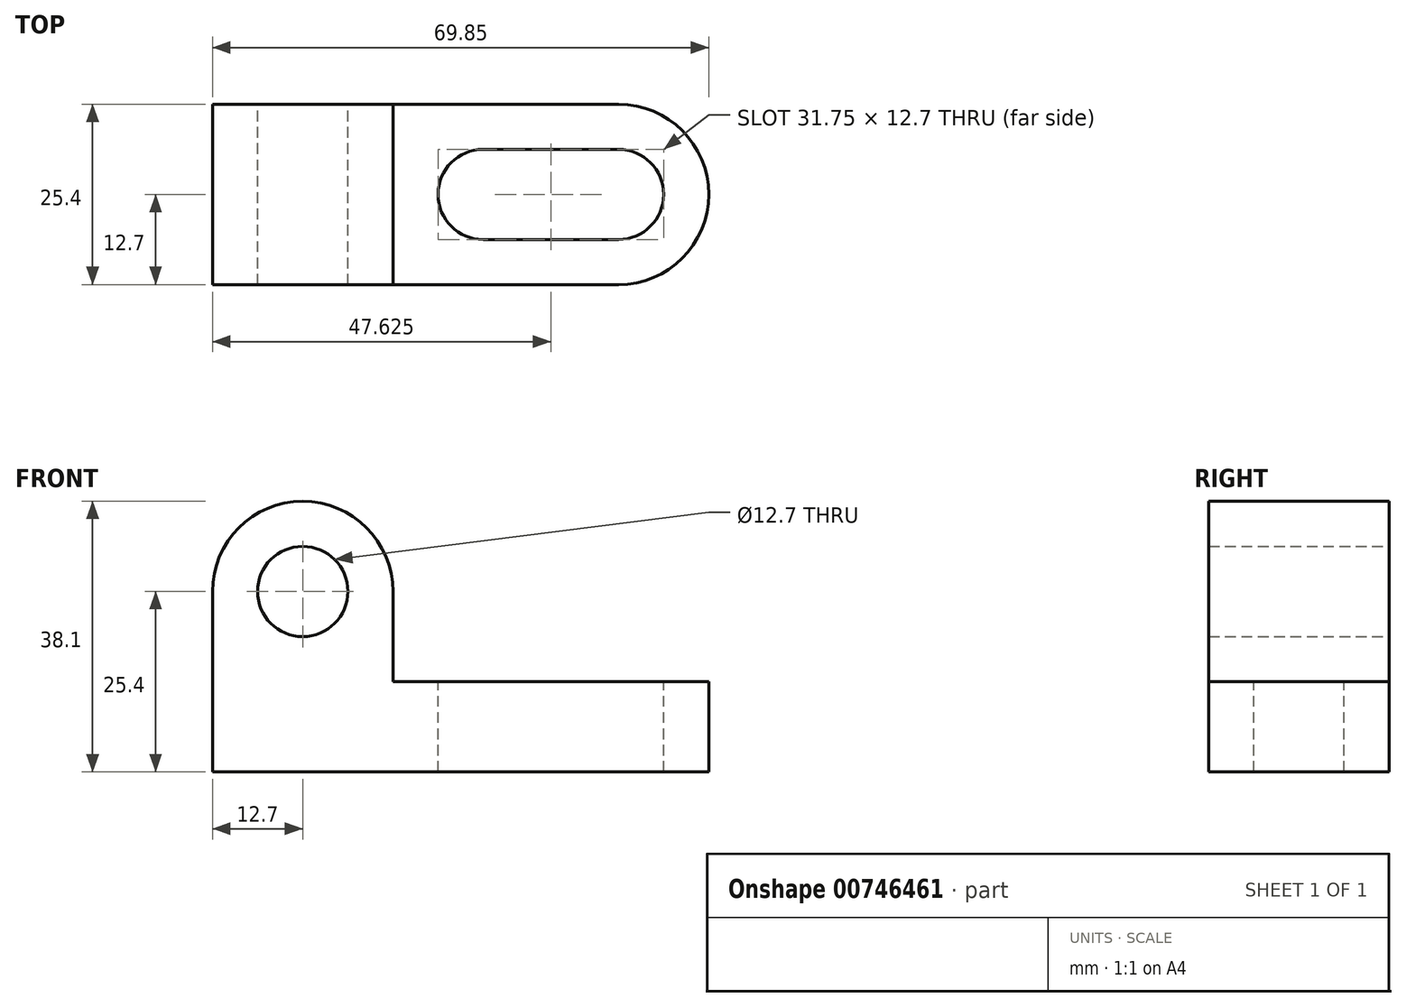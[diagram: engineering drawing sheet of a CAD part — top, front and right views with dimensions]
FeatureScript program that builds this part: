
annotation { "Feature Type Name" : "Feature", "Feature Type Description" : "" }
export const myFeature = defineFeature(function(context is Context, id is Id, definition is map)
    precondition{}
    {
        {
            var Q0;
            Q0=qCreatedBy(makeId("Front.planeOp"),FACE);
            var sketch = newSketch(context, id + "F0", { "sketchPlane" : qUnion([Q0])});
            skLineSegment(sketch, "E0", {"start": v(0, 0) * mm, "end": v(57.15, 0) * mm});
            skLineSegment(sketch, "E1", {"start": v(57.15, 0) * mm, "end": v(57.15, 12.7) * mm});
            skLineSegment(sketch, "E2", {"start": v(57.15, 12.7) * mm, "end": v(25.4, 12.7) * mm});
            skLineSegment(sketch, "E3", {"start": v(0, 0) * mm, "end": v(0, 25.4) * mm});
            skLineSegment(sketch, "E4", {"start": v(25.4, 12.7) * mm, "end": v(25.4, 25.4) * mm});
            skArc(sketch, "E5", {"start": v(25.4, 25.4) * mm, "mid": v(12.7, 38.1) * mm, "end": v(0, 25.4) * mm});
            skCircle(sketch, "E6", {"center": v(12.7, 25.4) * mm, "radius": 6.35 * mm});
            skLineSegment(sketch, "E7", {"start": v(25.4, 12.7) * mm, "end": v(25.4, 0) * mm});
            skSolve(sketch);
        }
        {
            var Q0;
            Q0=makeQuery(id+"F0.imprint","IMPRINT",FACE,{"disambiguationData":[TD([[makeQuery(id+"F0.imprint","IMPRINT",EDGE,{"derivedFrom":sQuery(id+"F0.wireOp",EDGE,"E0")}),1.0]])]});
            extrude(context, id + "F1", {"entities" : qUnion([Q0]), "depth" : 25.4 * mm, "offsetDistance" : 25.4 * mm});
        }
        {
            var Q0;
            Q0=makeQuery(id+"F1.opExtrude","SWEPT_FACE",FACE,{"disambiguationData":[OSD([sQuery(id+"F0.wireOp",EDGE,"E2")])]});
            var sketch = newSketch(context, id + "F2", { "sketchPlane" : qUnion([Q0])});
            skArc(sketch, "E8", {"start": v(57.15, -25.4) * mm, "mid": v(69.85, -12.7) * mm, "end": v(57.15, 0) * mm});
            skLineSegment(sketch, "E9", {"start": v(57.15, -6.35) * mm, "end": v(38.1, -6.35) * mm});
            skLineSegment(sketch, "E10", {"start": v(57.15, -19.05) * mm, "end": v(38.1, -19.05) * mm});
            skArc(sketch, "E11", {"start": v(38.1, -6.35) * mm, "mid": v(31.75, -12.7) * mm, "end": v(38.1, -19.05) * mm});
            skArc(sketch, "E12", {"start": v(57.15, -19.05) * mm, "mid": v(63.5, -12.7) * mm, "end": v(57.15, -6.35) * mm});
            skSolve(sketch);
        }
        {
            var Q0;
            {var subQ0=sQuery(id+"F2.wireOp",EDGE,"E8");Q0=makeQuery(id+"F2.imprint","IMPRINT",FACE,{"disambiguationData":[TD([[makeQuery(id+"F2.imprint","IMPRINT",EDGE,{"derivedFrom":subQ0}),1.0]])]});}
            extrude(context, id + "F3", {"entities" : qUnion([Q0]), "operationType" : NewBodyOperationType.ADD, "oppositeDirection" : true, "depth" : 12.7 * mm, "offsetDistance" : 25.4 * mm});
        }
        {
            var Q0;
            Q0 = qSketchRegion(id + "F0", true);
            extrude(context, id + "F4", {"entities" : qUnion([Q0]), "operationType" : NewBodyOperationType.ADD, "depth" : 25.4 * mm, "offsetDistance" : 25.4 * mm});
        }
        {
            var Q0;
            Q0 = qSketchRegion(id + "F2", true);
            extrude(context, id + "F5", {"entities" : qUnion([Q0]), "operationType" : NewBodyOperationType.REMOVE, "oppositeDirection" : true, "depth" : 25.4 * mm, "offsetDistance" : 25.4 * mm});
        }
    });
